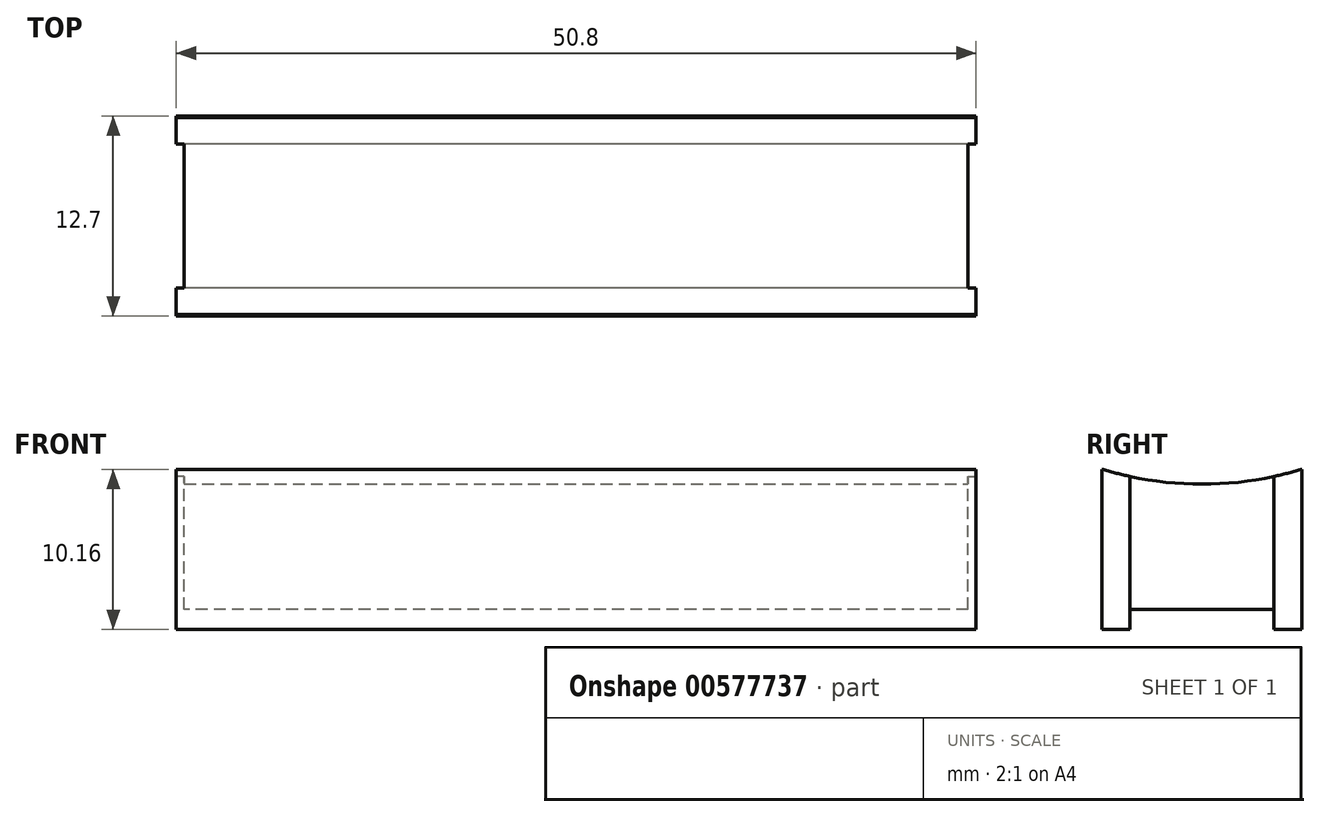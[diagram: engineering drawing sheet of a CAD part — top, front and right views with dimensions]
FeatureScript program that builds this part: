
annotation { "Feature Type Name" : "Feature", "Feature Type Description" : "" }
export const myFeature = defineFeature(function(context is Context, id is Id, definition is map)
    precondition{}
    {
        {
            var Q0;
            Q0=qCreatedBy(makeId("Top.planeOp"),FACE);
            var sketch = newSketch(context, id + "F0", { "sketchPlane" : qUnion([Q0])});
            skLineSegment(sketch, "E0.bottom", {"start": v(0, 0) * mm, "end": v(-50.8, 0) * mm});
            skLineSegment(sketch, "E0.top", {"start": v(0, 12.7) * mm, "end": v(-50.8, 12.7) * mm});
            skLineSegment(sketch, "E0.left", {"start": v(0, 0) * mm, "end": v(0, 12.7) * mm});
            skLineSegment(sketch, "E0.right", {"start": v(-50.8, 0) * mm, "end": v(-50.8, 12.7) * mm});
            skSolve(sketch);
        }
        {
            var Q0;
            Q0=makeQuery(id+"F0.imprint","IMPRINT",FACE,{"disambiguationData":[TD([[makeQuery(id+"F0.imprint","IMPRINT",EDGE,{"derivedFrom":sQuery(id+"F0.wireOp",EDGE,"E0.bottom")}),-1.0]])]});
            extrude(context, id + "F1", {"entities" : qUnion([Q0]), "depth" : 10.16 * mm, "offsetDistance" : 25.4 * mm});
        }
        {
            var Q0;
            Q0=qCreatedBy(makeId("Top.planeOp"),FACE);
            var sketch = newSketch(context, id + "F2", { "sketchPlane" : qUnion([Q0])});
            skLineSegment(sketch, "E1.bottom", {"start": v(0, 10.92) * mm, "end": v(-51.66, 10.92) * mm});
            skLineSegment(sketch, "E1.top", {"start": v(0, 1.78) * mm, "end": v(-51.66, 1.78) * mm});
            skLineSegment(sketch, "E1.left", {"start": v(0, 10.92) * mm, "end": v(0, 1.78) * mm});
            skLineSegment(sketch, "E1.right", {"start": v(-51.66, 10.92) * mm, "end": v(-51.66, 1.78) * mm});
            skSolve(sketch);
        }
        {
            var Q0;
            Q0=makeQuery(id+"F2.imprint","IMPRINT",FACE,{"disambiguationData":[TD([[makeQuery(id+"F2.imprint","IMPRINT",EDGE,{"derivedFrom":sQuery(id+"F2.wireOp",EDGE,"E1.bottom")}),1.0]])]});
            extrude(context, id + "F3", {"entities" : qUnion([Q0]), "operationType" : NewBodyOperationType.REMOVE, "depth" : 1.27 * mm, "offsetDistance" : 25.4 * mm});
        }
        {
            var Q0;
            Q0=makeQuery(id+"F1.opExtrude","SWEPT_FACE",FACE,{"disambiguationData":[OSD([sQuery(id+"F0.wireOp",EDGE,"E0.left")])]});
            var sketch = newSketch(context, id + "F4", { "sketchPlane" : qUnion([Q0])});
            skCircle(sketch, "E2", {"center": v(6.35, 30.82) * mm, "radius": 21.59 * mm});
            skPoint(sketch, "E2.centerSnap0", {"position": v(6.35, 10.16) * mm});
            skSolve(sketch);
        }
        {
            var Q0;
            {var subQ0=sQuery(id+"F4.wireOp",EDGE,"E2");var subQ1=makeQuery(id+"F1.opExtrude","CAP_EDGE",EDGE,{"disambiguationData":[OSD([sQuery(id+"F0.wireOp",EDGE,"E0.left")])],"isStart":false});var subQ2=makeQuery(id+"F4.imprint","INTERSECT",VERTEX,{"disambiguationData":[OD(0.0)],"derivedFrom":[subQ1,subQ0]});Q0=makeQuery(id+"F4.imprint","IMPRINT",FACE,{"disambiguationData":[TD([[makeQuery(id+"F4.imprint","IMPRINT",EDGE,{"disambiguationData":[TD([[subQ2,1.0]])],"derivedFrom":subQ0}),1.0]])]});}
            var Q1;
            {var subQ0=sQuery(id+"F4.wireOp",EDGE,"E2");var subQ1=makeQuery(id+"F1.opExtrude","CAP_EDGE",EDGE,{"disambiguationData":[OSD([sQuery(id+"F0.wireOp",EDGE,"E0.left")])],"isStart":false});var subQ2=makeQuery(id+"F4.imprint","INTERSECT",VERTEX,{"disambiguationData":[OD(0.0)],"derivedFrom":[subQ1,subQ0]});Q1=makeQuery(id+"F4.imprint","IMPRINT",FACE,{"disambiguationData":[TD([[makeQuery(id+"F4.imprint","IMPRINT",EDGE,{"disambiguationData":[TD([[subQ2,-1.0]])],"derivedFrom":subQ0}),1.0]])]});}
            extrude(context, id + "F5", {"entities" : qUnion([Q0, Q1]), "operationType" : NewBodyOperationType.REMOVE, "oppositeDirection" : true, "depth" : 59.69 * mm, "offsetDistance" : 25.4 * mm});
        }
        {
            var Q0;
            Q0=makeQuery(id+"F1.opExtrude","SWEPT_FACE",FACE,{"disambiguationData":[OSD([sQuery(id+"F0.wireOp",EDGE,"E0.left")])]});
            var sketch = newSketch(context, id + "F6", { "sketchPlane" : qUnion([Q0])});
            skLineSegment(sketch, "E3.bottom", {"start": v(1.78, 1.27) * mm, "end": v(10.92, 1.27) * mm});
            skLineSegment(sketch, "E3.top", {"start": v(1.78, 9.72) * mm, "end": v(10.92, 9.72) * mm});
            skLineSegment(sketch, "E3.left", {"start": v(1.78, 1.27) * mm, "end": v(1.78, 9.72) * mm});
            skLineSegment(sketch, "E3.right", {"start": v(10.92, 1.27) * mm, "end": v(10.92, 9.72) * mm});
            skSolve(sketch);
        }
        {
            var Q0;
            Q0=makeQuery(id+"F6.imprint","IMPRINT",FACE,{"disambiguationData":[TD([[makeQuery(id+"F6.imprint","IMPRINT",EDGE,{"derivedFrom":sQuery(id+"F6.wireOp",EDGE,"E3.bottom")}),-1.0]])]});
            extrude(context, id + "F7", {"entities" : qUnion([Q0]), "operationType" : NewBodyOperationType.REMOVE, "oppositeDirection" : true, "depth" : 0.5 * mm, "offsetDistance" : 25.4 * mm});
        }
        {
            var Q0;
            Q0=makeQuery(id+"F1.opExtrude","SWEPT_FACE",FACE,{"disambiguationData":[OSD([sQuery(id+"F0.wireOp",EDGE,"E0.right")])]});
            var sketch = newSketch(context, id + "F8", { "sketchPlane" : qUnion([Q0])});
            skLineSegment(sketch, "E4.bottom", {"start": v(-1.78, 1.27) * mm, "end": v(-10.92, 1.27) * mm});
            skLineSegment(sketch, "E4.top", {"start": v(-1.78, 9.72) * mm, "end": v(-10.92, 9.72) * mm});
            skLineSegment(sketch, "E4.left", {"start": v(-1.78, 1.27) * mm, "end": v(-1.78, 9.72) * mm});
            skLineSegment(sketch, "E4.right", {"start": v(-10.92, 1.27) * mm, "end": v(-10.92, 9.72) * mm});
            skSolve(sketch);
        }
        {
            var Q0;
            Q0=makeQuery(id+"F8.imprint","IMPRINT",FACE,{"disambiguationData":[TD([[makeQuery(id+"F8.imprint","IMPRINT",EDGE,{"derivedFrom":sQuery(id+"F8.wireOp",EDGE,"E4.bottom")}),-1.0]])]});
            extrude(context, id + "F9", {"entities" : qUnion([Q0]), "operationType" : NewBodyOperationType.REMOVE, "oppositeDirection" : true, "depth" : 0.5 * mm, "offsetDistance" : 25.4 * mm});
        }
    });
